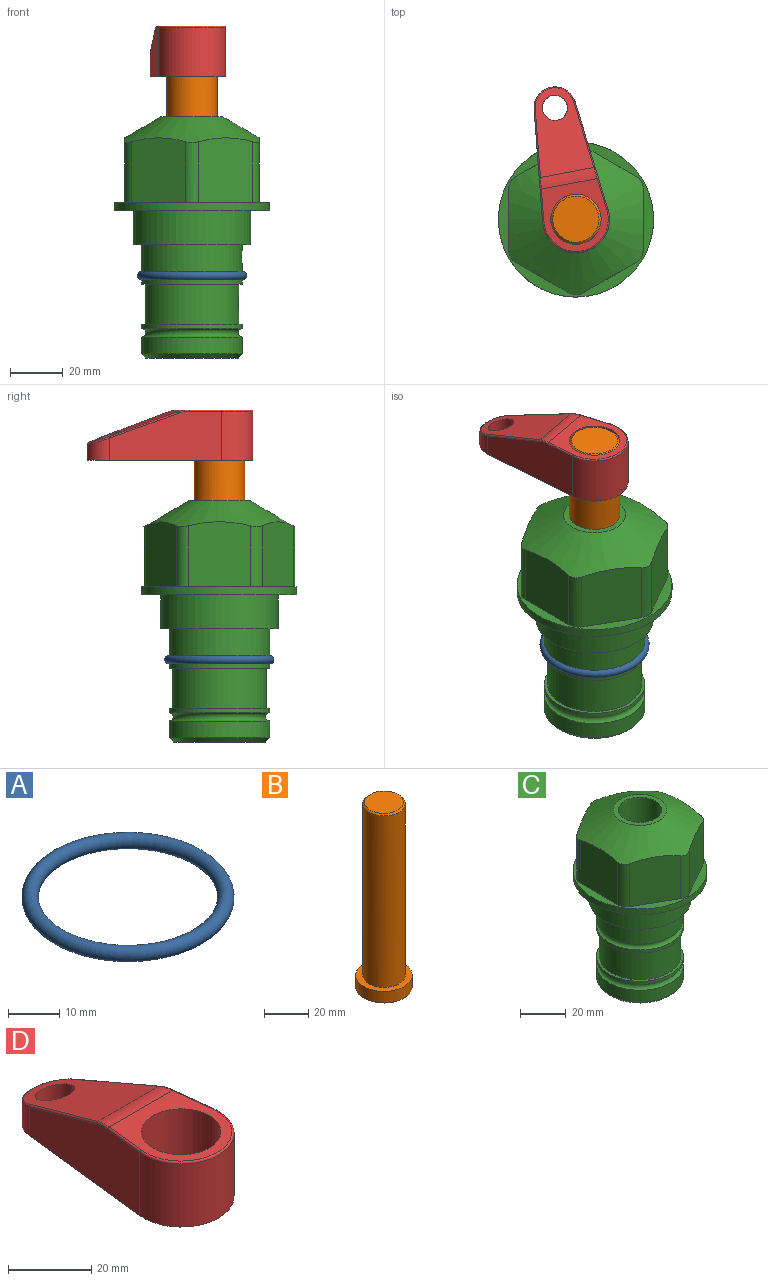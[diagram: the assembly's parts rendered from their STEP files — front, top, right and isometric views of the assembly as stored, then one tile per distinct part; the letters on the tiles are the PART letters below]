
ASSEMBLY  parts=4 mates=2
PART A: 1 faces, bbox 44.7x44.7x3.2 mm
  f0: torus R=19.05mm, axis (0,0,1), area 1193.9mm2
PART B: 6 faces, bbox 25.4x25.4x101.6 mm
  f0: plane 17.46x17.46mm, normal (0,0,1), area 239.5mm2, adj f5
  f1: plane 25.4x25.4mm, normal (0,0,-1), area 506.7mm2, adj f2
  f2: cylinder r=12.7mm len=25.4mm, axis (0,0,1), area 506.7mm2, adj f1,f3
  f3: plane 25.4x25.4mm, normal (0,0,1), area 221.7mm2, adj f2,f4
  f4: cylinder r=9.53mm len=94.46mm, axis (0,0,1), area 5653mm2, adj f3,f5
  f5: cone r=8.73mm half-angle=45deg, axis (0,0,-1), area 64.4mm2, adj f0,f4
PART C: 36 faces, bbox 58.7x58.7x91.2 mm
  f0: cylinder r=17.78mm len=35.56mm, axis (0,0,1), area 1670.8mm2, adj f23,f24,f31
  f1: cylinder r=19.05mm len=38.1mm, axis (0,0,1), area 1191.9mm2, adj f26,f27,f30
  f2: plane 58.66x58.66mm, normal (0,0,-1), area 1150.6mm2, adj f3,f28
  f3: cylinder r=29.33mm len=58.66mm, axis (0,0,-1), area 585.1mm2, adj f2,f4
  f4: plane 58.66x58.66mm, normal (0,0,1), area 475.9mm2, adj f3,f5,f6,f7,f8,f9,f10,f11
  f5: plane 24.5x20.32mm, normal (-0.5,0.87,0), area 562.8mm2, adj f4,f15,f16,f17
  f6: plane 24.5x20.32mm, normal (0.5,0.87,0), area 562.8mm2, adj f4,f14,f15,f17
  f7: plane 24.5x23.48mm, normal (1,0,0), area 562.8mm2, adj f4,f13,f14,f17
  f8: plane 24.5x20.32mm, normal (0.5,-0.87,0), area 562.8mm2, adj f4,f12,f13,f17
  f9: plane 24.5x20.32mm, normal (-0.5,-0.87,0), area 562.8mm2, adj f4,f11,f12,f17
  f10: plane 24.5x23.48mm, normal (-1,0,0), area 562.8mm2, adj f4,f11,f16,f17
  f11: cylinder r=5.08mm len=23.01mm, axis (0,0,-1), area 121.2mm2, adj f4,f9,f10,f17
  f12: cylinder r=5.08mm len=23.01mm, axis (0,0,-1), area 121.2mm2, adj f4,f8,f9,f17
  f13: cylinder r=5.08mm len=23.01mm, axis (0,0,-1), area 121.2mm2, adj f4,f7,f8,f17
  f14: cylinder r=5.08mm len=23.01mm, axis (0,0,-1), area 121.2mm2, adj f4,f6,f7,f17
  f15: cylinder r=5.08mm len=23.01mm, axis (0,0,-1), area 121.2mm2, adj f4,f5,f6,f17
  f16: cylinder r=5.08mm len=23.01mm, axis (0,0,-1), area 121.2mm2, adj f4,f5,f10,f17
  f17: cone r=11.73mm half-angle=60deg, axis (0,0,-1), area 2071.8mm2, adj f5,f6,f7,f8,f9,f10,f11,f12
  f18: plane 23.46x23.46mm, normal (0,0,1), area 147.4mm2, adj f17,f35
  f19: plane 34.93x34.93mm, normal (0,0,-1), area 958mm2, adj f29
  f20: cylinder r=19.05mm len=38.1mm, axis (0,0,1), area 760.1mm2, adj f21,f29
  f21: torus R=19.05mm, axis (0,0,1), area 565.3mm2, adj f20,f22
  f22: cylinder r=19.05mm len=38.1mm, axis (0,0,1), area 190mm2, adj f21,f23
  f23: plane 38.1x38.1mm, normal (0,0,1), area 146.9mm2, adj f0,f22
  f24: plane 38.1x38.1mm, normal (0,0,-1), area 146.9mm2, adj f0,f25
  f25: cylinder r=19.05mm len=38.1mm, axis (0,0,1), area 190mm2, adj f24,f26
  f26: torus R=19.05mm, axis (0,0,1), area 565.3mm2, adj f1,f25
  f27: plane 44.45x44.45mm, normal (0,0,-1), area 411.7mm2, adj f1,f28
  f28: cylinder r=22.23mm len=44.45mm, axis (0,0,1), area 1773.5mm2, adj f2,f27
  f29: cone r=19.05mm half-angle=45deg, axis (0,0,1), area 257.5mm2, adj f19,f20
  f30: cylinder r=3.17mm len=6.75mm, axis (-1,0,0), area 128mm2, adj f1,f33
  f31: cylinder r=3.17mm len=6.35mm, axis (-1,0,0), area 102.5mm2, adj f0,f33
  f32: plane 25.4x25.4mm, normal (0,0,1), area 506.7mm2, adj f33
  f33: cylinder r=12.7mm len=66.42mm, axis (0,0,-1), area 5236.2mm2, adj f30,f31,f32,f34
  f34: cone r=9.53mm half-angle=30deg, axis (0,0,-1), area 443.4mm2, adj f33,f35
  f35: cylinder r=9.53mm len=19.05mm, axis (0,0,-1), area 849mm2, adj f18,f34
PART D: 44 faces, bbox 27.5x64.5x19.1 mm
  f0: plane 2.3x0.95mm, normal (0,0,-1), area 1mm2, adj f25,f30,f34
  f1: plane 63.5x25.4mm, normal (0,0,-1), area 561.7mm2, adj f2,f3,f4,f5,f6,f7,f19,f20
  f2: cylinder r=12.7mm len=25.4mm, axis (0,0,-1), area 792.2mm2, adj f1,f3,f5,f13
  f3: plane 42.33x18.54mm, normal (0.99,0.11,0), area 647mm2, adj f1,f2,f4,f11,f12,f14
  f4: cylinder r=7.94mm len=15.78mm, axis (0,0,-1), area 158.6mm2, adj f1,f3,f5,f16
  f5: plane 42.33x18.54mm, normal (-0.99,0.11,0), area 647mm2, adj f1,f2,f4,f15,f17,f18
  f6: cylinder r=9.53mm len=19.05mm, axis (0,0,-1), area 1140.1mm2, adj f1,f8
  f7: cylinder r=4.76mm len=10.98mm, axis (0,0,-1), area 276.1mm2, adj f1,f9
  f8: plane 25.83x24.38mm, normal (0,0,1), area 262.2mm2, adj f6,f10,f11,f13,f15
  f9: plane 32.49x20.55mm, normal (0,0.34,0.94), area 489.9mm2, adj f7,f10,f14,f16,f18
  f10: cylinder r=12.7mm len=21.49mm, axis (-1,0,0), area 93.2mm2, adj f8,f9,f12,f17
  f11: cylinder r=0.51mm len=12.34mm, axis (0.11,-0.99,0), area 9.9mm2, adj f3,f8,f12,f13
  f12: bspline ~7.62x1.64mm, area 3.5mm2, adj f3,f10,f11,f14
  f13: torus R=12.19mm, axis (0,0,1), area 33.6mm2, adj f2,f8,f11,f15
  f14: cylinder r=0.51mm len=26.01mm, axis (0.1,-0.93,0.34), area 21.6mm2, adj f3,f9,f12,f16
  f15: cylinder r=0.51mm len=12.34mm, axis (0.11,0.99,0), area 9.9mm2, adj f5,f8,f13,f17
  f16: bspline ~15.78x7.05mm, area 15.7mm2, adj f4,f9,f14,f18
  f17: bspline ~7.62x1.64mm, area 3.5mm2, adj f5,f10,f15,f18
  f18: cylinder r=0.51mm len=26.01mm, axis (0.1,0.93,-0.34), area 21.6mm2, adj f5,f9,f16,f17
  f19: plane 21.6x14.29mm, normal (-0.99,-0.11,0), area 242.6mm2, adj f1,f26,f28,f34,f36,f38
  f20: plane 21.6x14.29mm, normal (0.99,-0.11,0), area 242.6mm2, adj f1,f27,f29,f37,f39,f41
  f21: cylinder r=12.7mm len=14.29mm, axis (0,0,-1), area 173.2mm2, adj f1,f26,f27,f30,f31,f33
  f22: cylinder r=7.94mm len=7.63mm, axis (0,0,-1), area 53.8mm2, adj f1,f28,f29,f42
  f23: plane 2.3x0.95mm, normal (0,0,-1), area 1mm2, adj f25,f33,f37
  f24: plane 17.94x12.32mm, normal (0,-0.34,-0.94), area 191.2mm2, adj f25,f38,f41,f42
  f25: cylinder r=9.53mm len=12.93mm, axis (-1,0,0), area 37.5mm2, adj f0,f23,f24,f31,f36,f39
  f26: cylinder r=1.59mm len=14.29mm, axis (0,0,-1), area 49mm2, adj f1,f19,f21,f32
  f27: cylinder r=1.59mm len=14.29mm, axis (0,0,-1), area 49mm2, adj f1,f20,f21,f35
  f28: cylinder r=1.59mm len=7.28mm, axis (0,0,-1), area 22.1mm2, adj f1,f19,f22,f40
  f29: cylinder r=1.59mm len=7.28mm, axis (0,0,-1), area 22.1mm2, adj f1,f20,f22,f43
  f30: torus R=14.29mm, axis (0,0,1), area 5.8mm2, adj f0,f21,f31,f32
  f31: bspline ~11.06x2.73mm, area 20.8mm2, adj f21,f25,f30,f33
  f32: sphere r=1.59mm, area 5.4mm2, adj f26,f30,f34
  f33: torus R=14.29mm, axis (0,0,1), area 5.8mm2, adj f21,f23,f31,f35
  f34: cylinder r=1.59mm len=1.68mm, axis (-0.11,0.99,0), area 2.4mm2, adj f0,f19,f32,f36
  f35: sphere r=1.59mm, area 5.4mm2, adj f27,f33,f37
  f36: bspline ~5.82x2.33mm, area 7.7mm2, adj f19,f25,f34,f38
  f37: cylinder r=1.59mm len=1.68mm, axis (0.11,0.99,0), area 2.4mm2, adj f20,f23,f35,f39
  f38: cylinder r=1.59mm len=18.33mm, axis (0.1,-0.93,0.34), area 46.7mm2, adj f19,f24,f36,f40
  f39: bspline ~5.82x2.33mm, area 7.7mm2, adj f20,f25,f37,f41
  f40: sphere r=1.59mm, area 3.6mm2, adj f28,f38,f42
  f41: cylinder r=1.59mm len=18.33mm, axis (0.1,0.93,-0.34), area 46.7mm2, adj f20,f24,f39,f43
  f42: bspline ~8.31x1.84mm, area 15.3mm2, adj f22,f24,f40,f43
  f43: sphere r=1.59mm, area 3.6mm2, adj f29,f41,f42
PLACE A at identity
PLACE B rot(axis=(0,0,1),10.7deg) t=(0,0,-3.72)mm
PLACE C at identity fixed
PLACE D rot(axis=(0,0,1),10.7deg) t=(0,0,50.89)mm
MATE fastened D.f2 <-> B.f2  axis (0,0,-1) through (0,0,69.94)mm
MATE cylindrical B.f2 <-> C.f0  axis (0,0,1) through (0,0,21.92)mm
